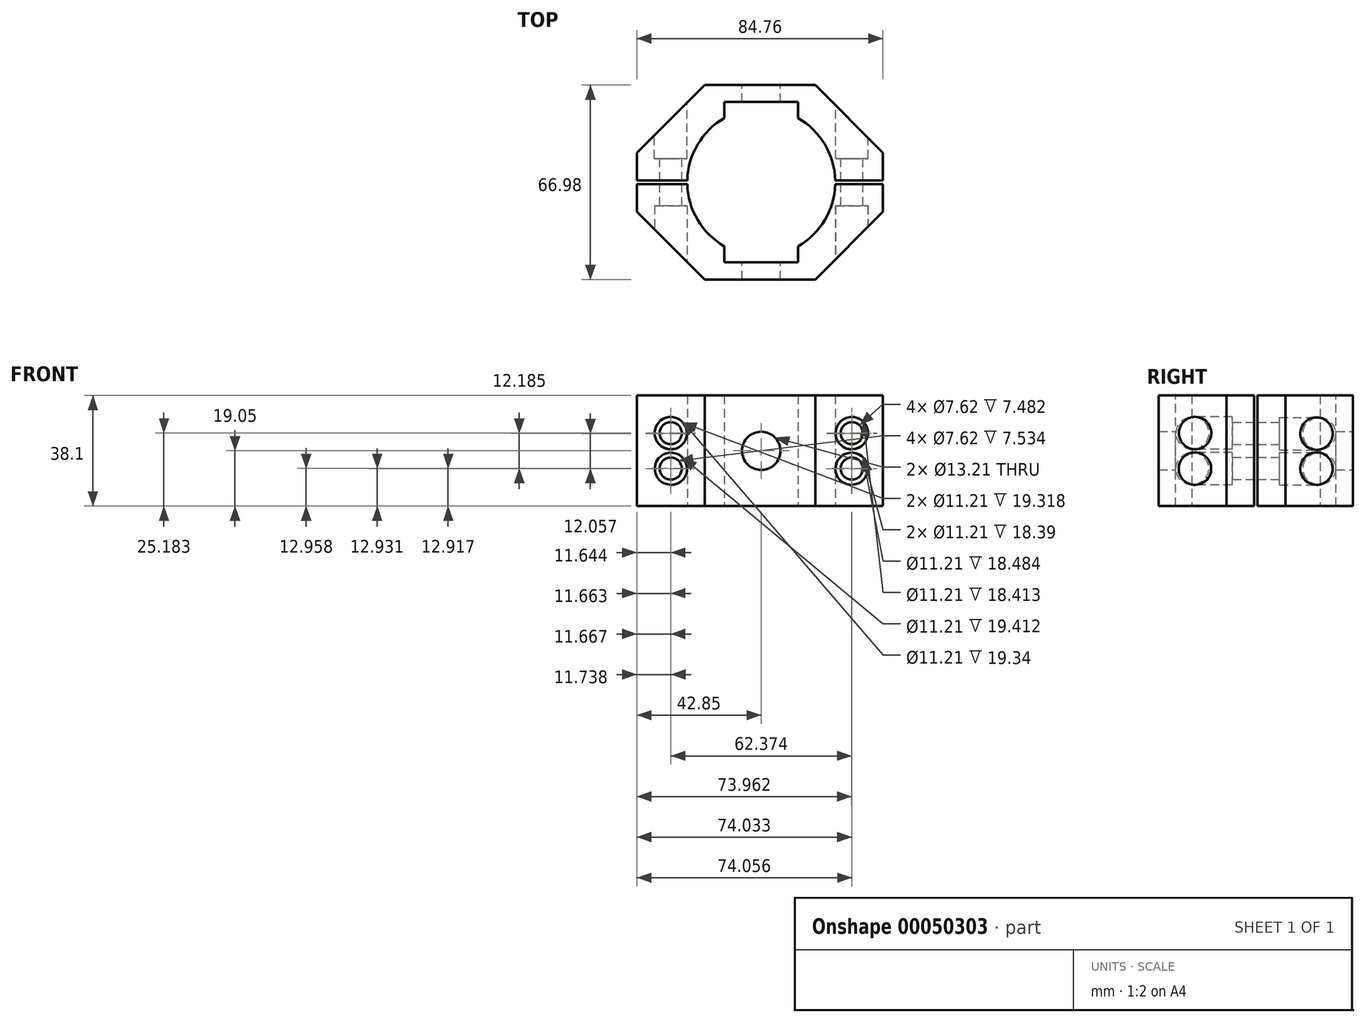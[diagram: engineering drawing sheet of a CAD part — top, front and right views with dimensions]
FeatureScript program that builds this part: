
annotation { "Feature Type Name" : "Feature", "Feature Type Description" : "" }
export const myFeature = defineFeature(function(context is Context, id is Id, definition is map)
    precondition{}
    {
        {
            var Q0;
            Q0=qCreatedBy(makeId("Top.planeOp"),FACE);
            var sketch = newSketch(context, id + "F0", { "sketchPlane" : qUnion([Q0])});
            skLineSegment(sketch, "E0", {"start": v(18.59, 33.5) * mm, "end": v(52.08, 0) * mm});
            skLineSegment(sketch, "E1", {"start": v(52.08, 0) * mm, "end": v(18.59, -33.5) * mm});
            skLineSegment(sketch, "E2", {"start": v(18.59, -33.5) * mm, "end": v(-19.51, -33.5) * mm});
            skLineSegment(sketch, "E3", {"start": v(-19.51, -33.5) * mm, "end": v(-53, 0) * mm});
            skLineSegment(sketch, "E4", {"start": v(-53, 0) * mm, "end": v(-19.51, 33.5) * mm});
            skCircle(sketch, "E5", {"center": v(0, 0) * mm, "radius": 25.48 * mm});
            skLineSegment(sketch, "E6", {"start": v(-19.51, 33.5) * mm, "end": v(18.59, 33.5) * mm});
            skLineSegment(sketch, "E7", {"start": v(0, 33.5) * mm, "end": v(0, 0) * mm});
            skLineSegment(sketch, "E8.bottom", {"start": v(-56.04, 16.89) * mm, "end": v(-42.85, 16.89) * mm});
            skLineSegment(sketch, "E8.top", {"start": v(-56.04, -17.81) * mm, "end": v(-42.85, -17.81) * mm});
            skLineSegment(sketch, "E8.left", {"start": v(-56.04, 16.89) * mm, "end": v(-56.04, -17.81) * mm});
            skLineSegment(sketch, "E8.right", {"start": v(-42.85, 16.89) * mm, "end": v(-42.85, -17.81) * mm});
            skLineSegment(sketch, "E9.left", {"start": v(41.9, 16.59) * mm, "end": v(41.9, -18.11) * mm});
            skLineSegment(sketch, "E9.bottom", {"start": v(41.9, 16.59) * mm, "end": v(54.8, 16.59) * mm});
            skLineSegment(sketch, "E9.right", {"start": v(54.8, 16.59) * mm, "end": v(54.8, -18.11) * mm});
            skLineSegment(sketch, "E9.top", {"start": v(41.9, -18.11) * mm, "end": v(54.8, -18.11) * mm});
            skLineSegment(sketch, "E10", {"start": v(-53, 0) * mm, "end": v(-42.85, 0) * mm});
            skLineSegment(sketch, "E11", {"start": v(41.92, 0) * mm, "end": v(52.08, 0) * mm});
            skSolve(sketch);
        }
        {
            var Q0;
            {var subQ13=sQuery(id+"F0.wireOp",EDGE,"E2");Q0=makeQuery(id+"F0.imprint","IMPRINT",FACE,{"disambiguationData":[TD([[makeQuery(id+"F0.imprint","IMPRINT",EDGE,{"derivedFrom":subQ13}),-1.0]])]});}
            extrude(context, id + "F1", {"entities" : qUnion([Q0]), "endBound" : BoundingType.SYMMETRIC, "depth" : 38.1 * mm});
        }
        {
            var Q0;
            Q0=makeQuery(id+"F1.opExtrude","SWEPT_FACE",FACE,{"disambiguationData":[OSD([sQuery(id+"F0.wireOp",EDGE,"E6")])]});
            var sketch = newSketch(context, id + "F2", { "sketchPlane" : qUnion([Q0])});
            skCircle(sketch, "E12.MirrorC", {"center": v(31.19, 6.1) * mm, "radius": 3.81 * mm});
            skCircle(sketch, "E13", {"center": v(-31.19, 6.1) * mm, "radius": 3.81 * mm});
            skCircle(sketch, "E14", {"center": v(-31.19, -6.1) * mm, "radius": 3.81 * mm});
            skCircle(sketch, "E15.MirrorC", {"center": v(31.19, -6.1) * mm, "radius": 3.81 * mm});
            skLineSegment(sketch, "E16", {"start": v(-31.19, 6.1) * mm, "end": v(-31.19, -6.1) * mm});
            skLineSegment(sketch, "E17", {"start": v(31.19, 6.1) * mm, "end": v(31.19, -6.1) * mm});
            skCircle(sketch, "E18", {"center": v(0, 0) * mm, "radius": 6.6 * mm});
            skLineSegment(sketch, "E19", {"start": v(31.19, 0) * mm, "end": v(-31.19, 0) * mm});
            skSolve(sketch);
        }
        {
            var Q0;
            Q0 = qSketchRegion(id + "F2", true);
            extrude(context, id + "F3", {"entities" : qUnion([Q0]), "operationType" : NewBodyOperationType.REMOVE, "endBound" : BoundingType.THROUGH_ALL, "oppositeDirection" : true, "depth" : 25.4 * mm});
        }
        {
            var Q0;
            Q0=makeQuery(id+"F1.opExtrude","SWEPT_FACE",FACE,{"disambiguationData":[OSD([sQuery(id+"F0.wireOp",EDGE,"E2")])]});
            var sketch = newSketch(context, id + "F4", { "sketchPlane" : qUnion([Q0])});
            skCircle(sketch, "E20", {"center": v(-31.18, 6.13) * mm, "radius": 5.6 * mm});
            skCircle(sketch, "E21", {"center": v(-31.11, -6.13) * mm, "radius": 5.6 * mm});
            skLineSegment(sketch, "E22", {"start": v(-31.18, 6.13) * mm, "end": v(-31.11, -6.13) * mm});
            skLineSegment(sketch, "E23", {"start": v(-31.15, 0) * mm, "end": v(18.59, 0) * mm});
            skCircle(sketch, "E24.MirrorC", {"center": v(31.11, -6.13) * mm, "radius": 5.6 * mm});
            skCircle(sketch, "E25.MirrorC", {"center": v(31.18, 6.13) * mm, "radius": 5.6 * mm});
            skSolve(sketch);
        }
        {
            var Q0;
            Q0 = qSketchRegion(id + "F4", true);
            extrude(context, id + "F5", {"entities" : qUnion([Q0]), "operationType" : NewBodyOperationType.REMOVE, "oppositeDirection" : true, "depth" : 25.4 * mm});
        }
        {
            var Q0;
            Q0=makeQuery(id+"F1.opExtrude","SWEPT_FACE",FACE,{"disambiguationData":[OSD([sQuery(id+"F0.wireOp",EDGE,"E6")])]});
            var sketch = newSketch(context, id + "F6", { "sketchPlane" : qUnion([Q0])});
            skCircle(sketch, "E26", {"center": v(-31.2, 5.94) * mm, "radius": 5.6 * mm});
            skCircle(sketch, "E27", {"center": v(-31.2, -6.12) * mm, "radius": 5.6 * mm});
            skLineSegment(sketch, "E28", {"start": v(-31.2, 5.94) * mm, "end": v(-31.2, -6.12) * mm});
            skCircle(sketch, "E29.MirrorC", {"center": v(31.2, 5.94) * mm, "radius": 5.6 * mm});
            skCircle(sketch, "E30.MirrorC", {"center": v(31.2, -6.12) * mm, "radius": 5.6 * mm});
            skLineSegment(sketch, "E31", {"start": v(31.2, 5.94) * mm, "end": v(31.2, -6.12) * mm});
            skLineSegment(sketch, "E32", {"start": v(31.2, -0.09) * mm, "end": v(-31.2, -0.09) * mm});
            skSolve(sketch);
        }
        {
            var Q0;
            Q0 = qSketchRegion(id + "F6", true);
            extrude(context, id + "F7", {"entities" : qUnion([Q0]), "operationType" : NewBodyOperationType.REMOVE, "oppositeDirection" : true, "depth" : 25.4 * mm});
        }
        {
            var Q0;
            Q0=makeQuery(id+"F1.opExtrude","CAP_FACE",FACE,{"disambiguationData":[OSD([sQuery(id+"F0.wireOp",EDGE,"E0"),sQuery(id+"F0.wireOp",EDGE,"E1"),sQuery(id+"F0.wireOp",EDGE,"E2"),sQuery(id+"F0.wireOp",EDGE,"E3"),sQuery(id+"F0.wireOp",EDGE,"E4"),sQuery(id+"F0.wireOp",EDGE,"E5"),sQuery(id+"F0.wireOp",EDGE,"E6"),sQuery(id+"F0.wireOp",EDGE,"E8.right"),sQuery(id+"F0.wireOp",EDGE,"E9.left")])],"isStart":true});
            var sketch = newSketch(context, id + "F8", { "sketchPlane" : qUnion([Q0])});
            skLineSegment(sketch, "E33.bottom", {"start": v(-49.62, 0.61) * mm, "end": v(60.64, 0.61) * mm});
            skLineSegment(sketch, "E33.top", {"start": v(-49.62, -0.56) * mm, "end": v(60.64, -0.56) * mm});
            skLineSegment(sketch, "E33.left", {"start": v(-49.62, 0.61) * mm, "end": v(-49.62, -0.56) * mm});
            skLineSegment(sketch, "E33.right", {"start": v(60.64, 0.61) * mm, "end": v(60.64, -0.56) * mm});
            skSolve(sketch);
        }
        {
            var Q0;
            Q0 = qSketchRegion(id + "F8", true);
            extrude(context, id + "F9", {"entities" : qUnion([Q0]), "operationType" : NewBodyOperationType.REMOVE, "endBound" : BoundingType.THROUGH_ALL, "oppositeDirection" : true, "depth" : 83.51 * mm});
        }
        {
            var Q0;
            {var subQ0=sQuery(id+"F0.wireOp",EDGE,"E6");var subQ1=sQuery(id+"F0.wireOp",EDGE,"E5");var subQ2=sQuery(id+"F0.wireOp",EDGE,"E4");var subQ3=sQuery(id+"F0.wireOp",EDGE,"E0");var subQ4=sQuery(id+"F0.wireOp",EDGE,"E8.right");var subQ5=sQuery(id+"F0.wireOp",EDGE,"E9.left");Q0=makeQuery(id+"F9.boolean.opBoolean","SPLIT",FACE,{"disambiguationData":[TD([makeQuery(id+"F1.opExtrude","SWEPT_FACE",FACE,{"disambiguationData":[OSD([subQ3])]})])],"derivedFrom":makeQuery(id+"F1.opExtrude","CAP_FACE",FACE,{"disambiguationData":[OSD([subQ3,sQuery(id+"F0.wireOp",EDGE,"E1"),sQuery(id+"F0.wireOp",EDGE,"E2"),sQuery(id+"F0.wireOp",EDGE,"E3"),subQ2,subQ1,subQ0,subQ4,subQ5])],"isStart":false})});}
            var sketch = newSketch(context, id + "F10", { "sketchPlane" : qUnion([Q0])});
            skLineSegment(sketch, "E34.bottom", {"start": v(-12.7, -21.31) * mm, "end": v(12.7, -21.31) * mm});
            skLineSegment(sketch, "E34.top", {"start": v(-12.7, -27.61) * mm, "end": v(12.7, -27.61) * mm});
            skLineSegment(sketch, "E34.left", {"start": v(-12.7, -21.31) * mm, "end": v(-12.7, -27.61) * mm});
            skLineSegment(sketch, "E34.right", {"start": v(12.7, -21.31) * mm, "end": v(12.7, -27.61) * mm});
            skLineSegment(sketch, "E35", {"start": v(0, 0) * mm, "end": v(0, -21.31) * mm});
            skLineSegment(sketch, "E36.MirrorCS", {"start": v(-12.7, 21.31) * mm, "end": v(12.7, 21.31) * mm});
            skLineSegment(sketch, "E37.MirrorCS", {"start": v(-12.7, 21.31) * mm, "end": v(-12.7, 27.61) * mm});
            skLineSegment(sketch, "E38.MirrorCS", {"start": v(12.7, 21.31) * mm, "end": v(12.7, 27.61) * mm});
            skLineSegment(sketch, "E39.MirrorCS", {"start": v(-12.7, 27.61) * mm, "end": v(12.7, 27.61) * mm});
            skSolve(sketch);
        }
        {
            var Q0;
            Q0 = qSketchRegion(id + "F10", true);
            extrude(context, id + "F11", {"entities" : qUnion([Q0]), "operationType" : NewBodyOperationType.REMOVE, "endBound" : BoundingType.THROUGH_ALL, "oppositeDirection" : true, "depth" : 25.4 * mm});
        }
        {
            var Q0;
            Q0=makeQuery(id+"F1.opExtrude","SWEPT_FACE",FACE,{"disambiguationData":[OSD([sQuery(id+"F0.wireOp",EDGE,"E6")])]});
            cPlane(context, id + "F12", {"entities" : qUnion([Q0]), "cplaneType" : CPlaneType.OFFSET, "offset" : 0 * mm, "width" : 152.4 * mm, "height" : 152.4 * mm});
        }
    });
